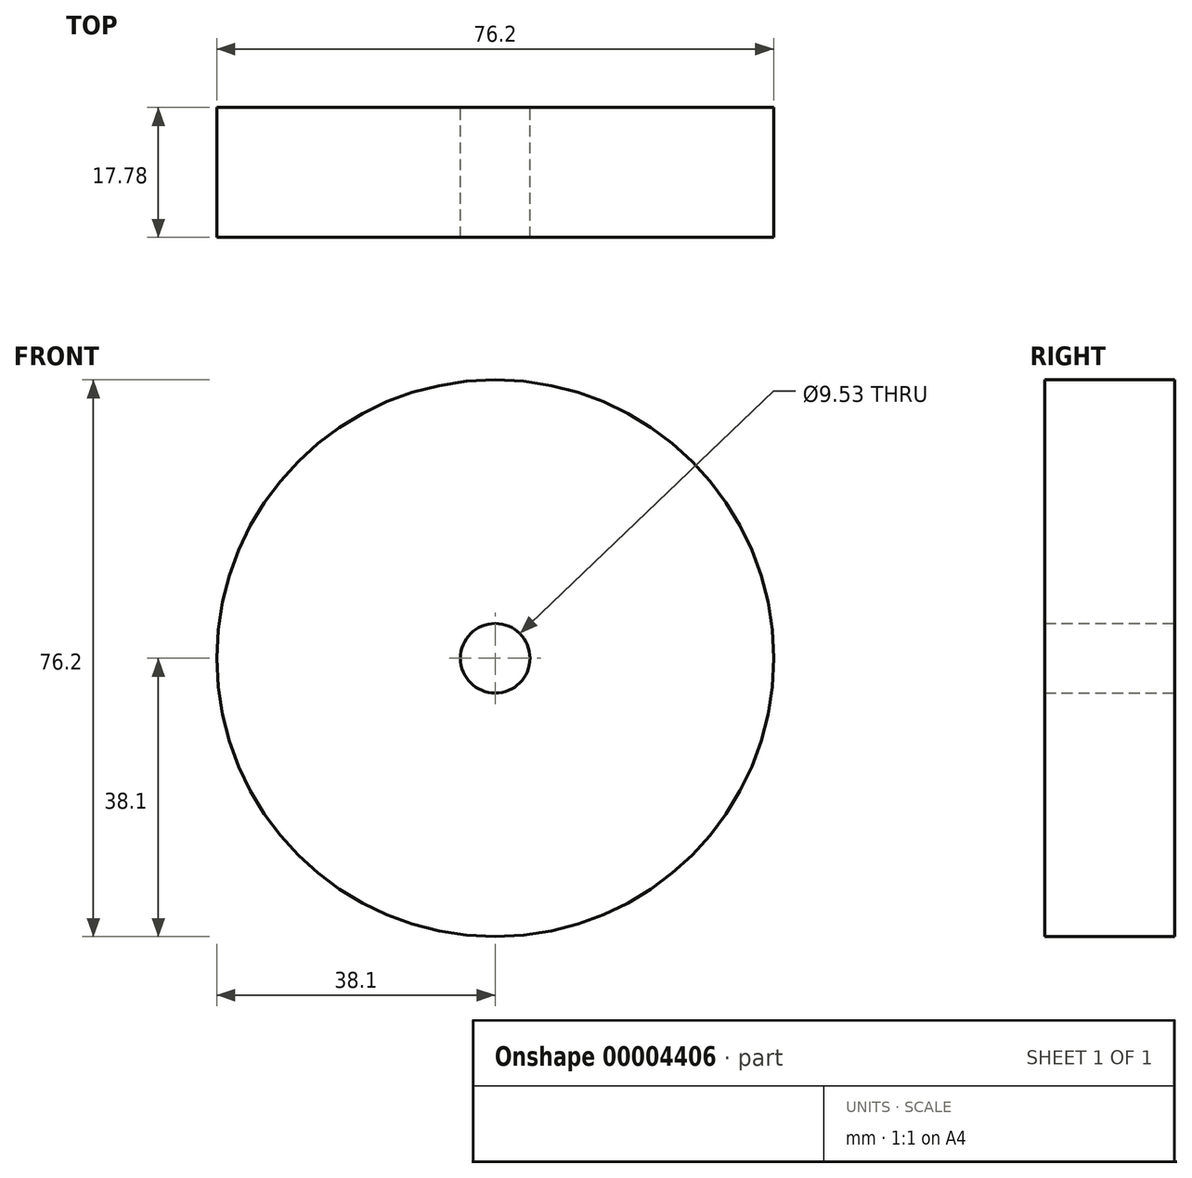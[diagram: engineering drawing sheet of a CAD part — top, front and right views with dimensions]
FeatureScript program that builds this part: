
annotation { "Feature Type Name" : "Feature", "Feature Type Description" : "" }
export const myFeature = defineFeature(function(context is Context, id is Id, definition is map)
    precondition{}
    {
        {
            var Q0;
            Q0=qCreatedBy(makeId("Front.planeOp"),FACE);
            var sketch = newSketch(context, id + "F0", { "sketchPlane" : qUnion([Q0])});
            skCircle(sketch, "E0", {"center": v(0, 0) * mm, "radius": 38.1 * mm});
            skCircle(sketch, "E1", {"center": v(0, 0) * mm, "radius": 4.76 * mm});
            skSolve(sketch);
        }
        {
            var Q0;
            Q0=makeQuery(id+"F0.imprint","IMPRINT",FACE,{"disambiguationData":[TD([[makeQuery(id+"F0.imprint","IMPRINT",EDGE,{"derivedFrom":sQuery(id+"F0.wireOp",EDGE,"E0")}),1.0]])]});
            extrude(context, id + "F1", {"entities" : qUnion([Q0]), "depth" : 17.78 * mm});
        }
    });
